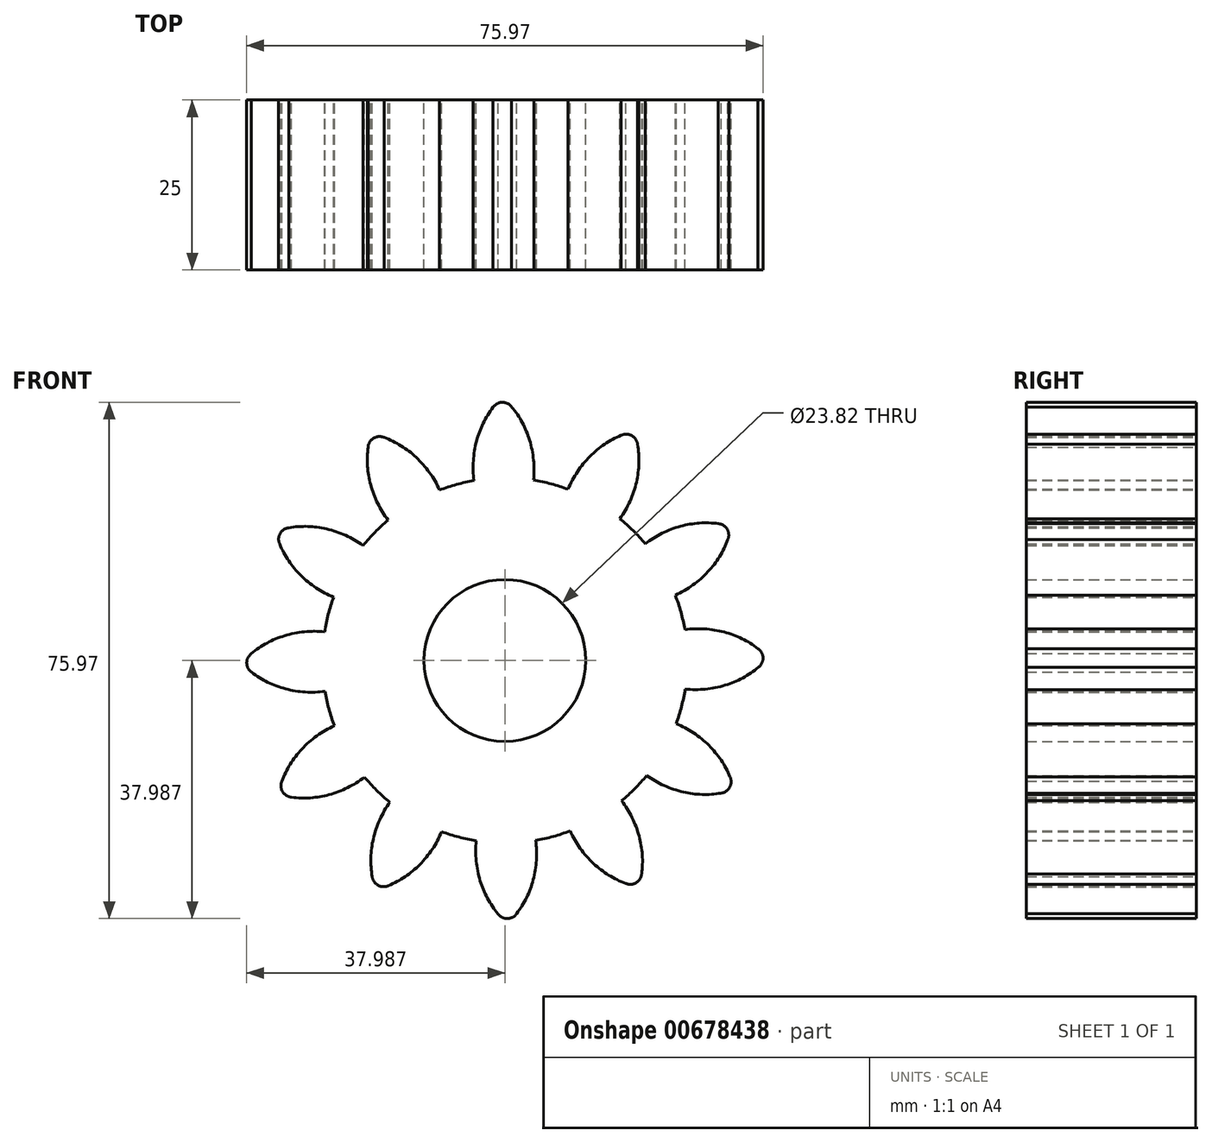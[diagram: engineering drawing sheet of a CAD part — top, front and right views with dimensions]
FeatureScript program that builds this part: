
annotation { "Feature Type Name" : "Feature", "Feature Type Description" : "" }
export const myFeature = defineFeature(function(context is Context, id is Id, definition is map)
    precondition{}
    {
        {
            var Q0;
            Q0=qCreatedBy(makeId("Front.planeOp"),FACE);
            var sketch = newSketch(context, id + "F0", { "sketchPlane" : qUnion([Q0])});
            skCircle(sketch, "E0", {"center": v(0, 0) * mm, "radius": 31.75 * mm, "construction": true});
            skCircle(sketch, "E1", {"center": v(0.07, 0.07) * mm, "radius": 29.34 * mm, "construction": true});
            skCircle(sketch, "E2", {"center": v(0.07, 0.07) * mm, "radius": 26.86 * mm});
            skArc(sketch, "E3", {"start": v(3.7, 32.49) * mm, "mid": v(2.63, 35.07) * mm, "end": v(1.07, 37.38) * mm});
            skArc(sketch, "E4", {"start": v(4.27, 26.42) * mm, "mid": v(4.3, 29.48) * mm, "end": v(3.7, 32.49) * mm});
            skArc(sketch, "E5.MirrorCS", {"start": v(-4.1, 32.34) * mm, "mid": v(-3.14, 34.95) * mm, "end": v(-1.67, 37.32) * mm});
            skArc(sketch, "E6.MirrorCS", {"start": v(-4.44, 26.24) * mm, "mid": v(-4.58, 29.3) * mm, "end": v(-4.1, 32.34) * mm});
            skArc(sketch, "E7", {"start": v(1.07, 37.38) * mm, "mid": v(-0.31, 38.05) * mm, "end": v(-1.67, 37.32) * mm});
            skCircle(sketch, "E8", {"center": v(0.07, 0.07) * mm, "radius": 11.9 * mm});
            skSolve(sketch);
        }
        {
            var Q0;
            {var subQ2=sQuery(id+"F0.wireOp",EDGE,"E3");Q0=makeQuery(id+"F0.imprint","IMPRINT",FACE,{"disambiguationData":[TD([[makeQuery(id+"F0.imprint","IMPRINT",EDGE,{"derivedFrom":subQ2}),1.0]])]});}
            var Q1;
            {var subQ0=sQuery(id+"F0.wireOp",EDGE,"E2");var subQ1=makeQuery(id+"F0.imprint","INTERSECT",VERTEX,{"derivedFrom":[subQ0,sQuery(id+"F0.wireOp",EDGE,"E4")]});Q1=makeQuery(id+"F0.imprint","IMPRINT",FACE,{"disambiguationData":[TD([[makeQuery(id+"F0.imprint","IMPRINT",EDGE,{"disambiguationData":[TD([[subQ1,-1.0]])],"derivedFrom":subQ0}),1.0]])]});}
            extrude(context, id + "F1", {"entities" : qUnion([Q0, Q1]), "depth" : 25 * mm, "offsetDistance" : 25 * mm});
        }
        {
            var Q0;
            Q0=makeQuery(id+"F1.opExtrude","SWEPT_BODY",BODY,{"disambiguationData":[OSD([sQuery(id+"F0.wireOp",EDGE,"E2"),sQuery(id+"F0.wireOp",EDGE,"E3"),sQuery(id+"F0.wireOp",EDGE,"E4"),sQuery(id+"F0.wireOp",EDGE,"E5.MirrorCS"),sQuery(id+"F0.wireOp",EDGE,"E6.MirrorCS"),sQuery(id+"F0.wireOp",EDGE,"E7")])]});
            var Q1;
            Q1=makeQuery(id+"F1.opExtrude","SWEPT_FACE",FACE,{"disambiguationData":[OSD([sQuery(id+"F0.wireOp",EDGE,"E2")])]});
            circularPattern(context, id + "F2", {"operationType" : NewBodyOperationType.ADD, "entities" : qUnion([Q0]), "axis" : qUnion([Q1]), "angle" : 360 * degree, "instanceCount" : 12, "equalSpace" : true});
        }
    });
